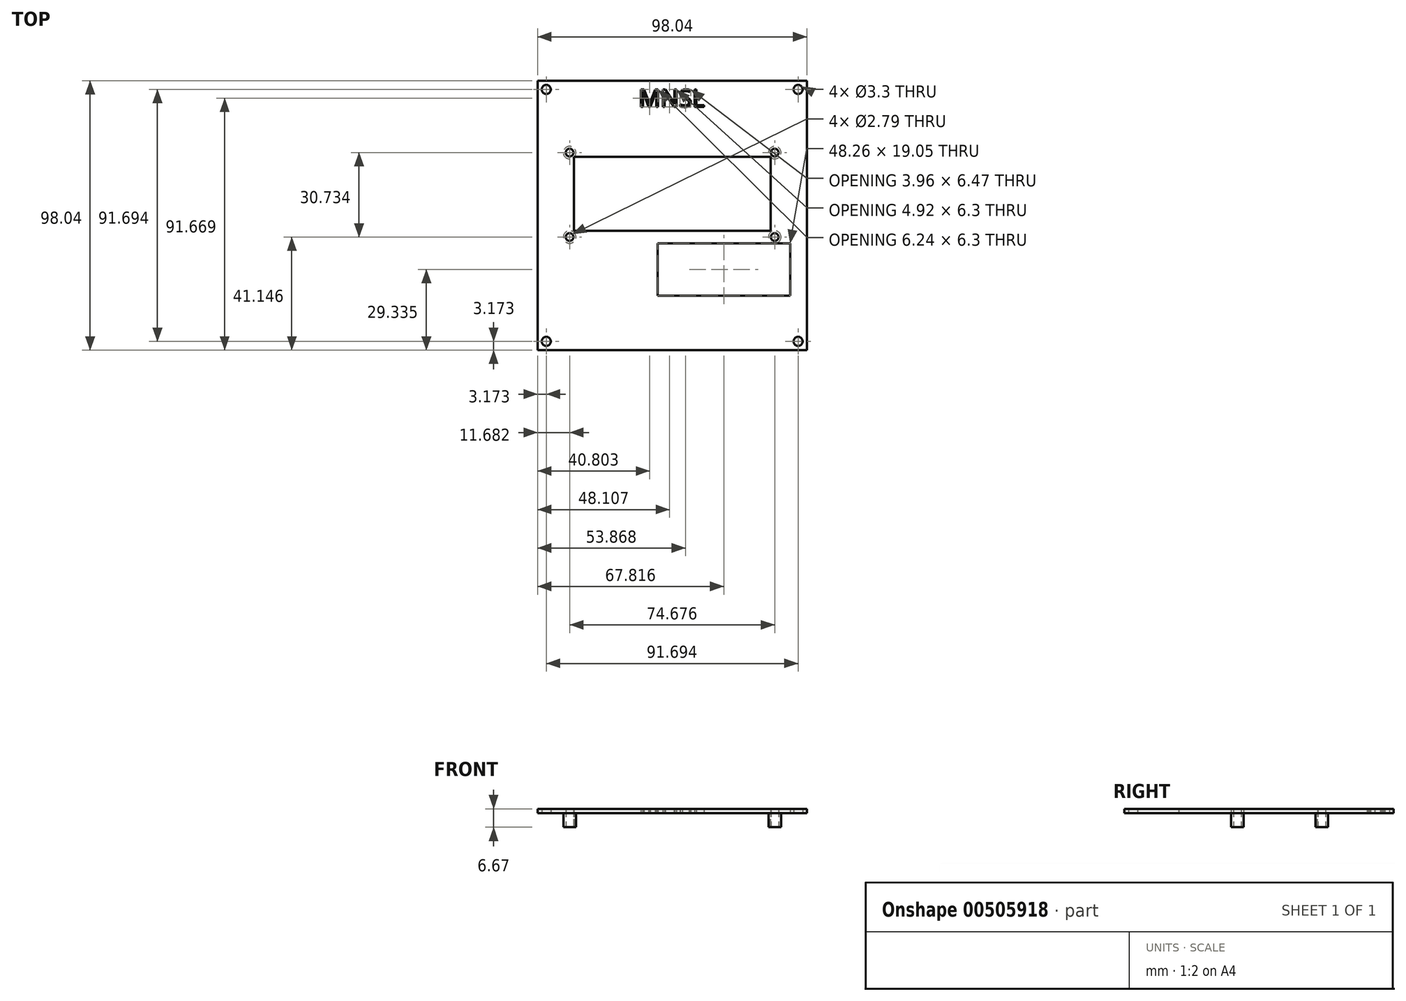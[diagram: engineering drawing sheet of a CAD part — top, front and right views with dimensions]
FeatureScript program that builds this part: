
annotation { "Feature Type Name" : "Feature", "Feature Type Description" : "" }
export const myFeature = defineFeature(function(context is Context, id is Id, definition is map)
    precondition{}
    {
        {
            var Q0;
            Q0=qCreatedBy(makeId("Top.planeOp"),FACE);
            var sketch = newSketch(context, id + "F0", { "sketchPlane" : qUnion([Q0])});
            skLineSegment(sketch, "E0.bottom", {"start": v(49.02, 49.02) * mm, "end": v(-49.02, 49.02) * mm});
            skLineSegment(sketch, "E0.top", {"start": v(49.02, -49.02) * mm, "end": v(-49.02, -49.02) * mm});
            skLineSegment(sketch, "E0.left", {"start": v(49.02, 49.02) * mm, "end": v(49.02, -49.02) * mm});
            skLineSegment(sketch, "E0.right", {"start": v(-49.02, 49.02) * mm, "end": v(-49.02, -49.02) * mm});
            skPoint(sketch, "E0.middle", {"position": v(0, 0) * mm});
            skLineSegment(sketch, "E1.bottom", {"start": v(49.02, 49.02) * mm, "end": v(42.67, 49.02) * mm, "construction": true});
            skLineSegment(sketch, "E1.top", {"start": v(49.02, 42.67) * mm, "end": v(42.67, 42.67) * mm, "construction": true});
            skLineSegment(sketch, "E1.left", {"start": v(49.02, 49.02) * mm, "end": v(49.02, 42.67) * mm, "construction": true});
            skLineSegment(sketch, "E1.right", {"start": v(42.67, 49.02) * mm, "end": v(42.67, 42.67) * mm, "construction": true});
            skLineSegment(sketch, "E2.bottom", {"start": v(-49.02, 49.02) * mm, "end": v(-42.67, 49.02) * mm, "construction": true});
            skLineSegment(sketch, "E2.top", {"start": v(-49.02, 42.67) * mm, "end": v(-42.67, 42.67) * mm, "construction": true});
            skLineSegment(sketch, "E2.left", {"start": v(-49.02, 49.02) * mm, "end": v(-49.02, 42.67) * mm, "construction": true});
            skLineSegment(sketch, "E2.right", {"start": v(-42.67, 49.02) * mm, "end": v(-42.67, 42.67) * mm, "construction": true});
            skLineSegment(sketch, "E3.bottom", {"start": v(-49.02, -49.02) * mm, "end": v(-42.67, -49.02) * mm, "construction": true});
            skLineSegment(sketch, "E3.top", {"start": v(-49.02, -42.67) * mm, "end": v(-42.67, -42.67) * mm, "construction": true});
            skLineSegment(sketch, "E3.left", {"start": v(-49.02, -49.02) * mm, "end": v(-49.02, -42.67) * mm, "construction": true});
            skLineSegment(sketch, "E3.right", {"start": v(-42.67, -49.02) * mm, "end": v(-42.67, -42.67) * mm, "construction": true});
            skLineSegment(sketch, "E4.bottom", {"start": v(49.02, -49.02) * mm, "end": v(42.67, -49.02) * mm, "construction": true});
            skLineSegment(sketch, "E4.top", {"start": v(49.02, -42.67) * mm, "end": v(42.67, -42.67) * mm, "construction": true});
            skLineSegment(sketch, "E4.left", {"start": v(49.02, -49.02) * mm, "end": v(49.02, -42.67) * mm, "construction": true});
            skLineSegment(sketch, "E4.right", {"start": v(42.67, -49.02) * mm, "end": v(42.67, -42.67) * mm, "construction": true});
            skLineSegment(sketch, "E5", {"start": v(-42.67, -42.67) * mm, "end": v(-49.02, -49.02) * mm, "construction": true});
            skLineSegment(sketch, "E6", {"start": v(-42.67, 42.67) * mm, "end": v(-49.02, 49.02) * mm, "construction": true});
            skLineSegment(sketch, "E7", {"start": v(49.02, 49.02) * mm, "end": v(42.67, 42.67) * mm, "construction": true});
            skLineSegment(sketch, "E8", {"start": v(49.02, -49.02) * mm, "end": v(42.67, -42.67) * mm, "construction": true});
            skCircle(sketch, "E9", {"center": v(45.85, -45.85) * mm, "radius": 1.65 * mm});
            skCircle(sketch, "E10", {"center": v(45.85, 45.85) * mm, "radius": 1.65 * mm});
            skCircle(sketch, "E11", {"center": v(-45.85, 45.85) * mm, "radius": 1.65 * mm});
            skCircle(sketch, "E12", {"center": v(-45.85, -45.85) * mm, "radius": 1.65 * mm});
            skLineSegment(sketch, "E13.bottom", {"start": v(39.88, 25.4) * mm, "end": v(-39.88, 25.4) * mm, "construction": true});
            skLineSegment(sketch, "E13.top", {"start": v(39.88, -25.4) * mm, "end": v(-39.88, -25.4) * mm, "construction": true});
            skLineSegment(sketch, "E13.left", {"start": v(39.88, 25.4) * mm, "end": v(39.88, -25.4) * mm, "construction": true});
            skLineSegment(sketch, "E13.right", {"start": v(-39.88, 25.4) * mm, "end": v(-39.88, -25.4) * mm, "construction": true});
            skLineSegment(sketch, "E14.bottom", {"start": v(-39.88, 25.4) * mm, "end": v(-37.34, 25.4) * mm, "construction": true});
            skLineSegment(sketch, "E14.top", {"start": v(-39.88, 22.86) * mm, "end": v(-37.34, 22.86) * mm, "construction": true});
            skLineSegment(sketch, "E14.left", {"start": v(-39.88, 25.4) * mm, "end": v(-39.88, 22.86) * mm, "construction": true});
            skLineSegment(sketch, "E14.right", {"start": v(-37.34, 25.4) * mm, "end": v(-37.34, 22.86) * mm, "construction": true});
            skCircle(sketch, "E15", {"center": v(-37.34, 22.86) * mm, "radius": 1.4 * mm});
            skLineSegment(sketch, "E16.bottom", {"start": v(-37.34, 22.86) * mm, "end": v(37.34, 22.86) * mm, "construction": true});
            skLineSegment(sketch, "E16.top", {"start": v(-37.34, -7.87) * mm, "end": v(37.34, -7.87) * mm, "construction": true});
            skLineSegment(sketch, "E16.left", {"start": v(-37.34, 22.86) * mm, "end": v(-37.34, -7.87) * mm, "construction": true});
            skLineSegment(sketch, "E16.right", {"start": v(37.34, 22.86) * mm, "end": v(37.34, -7.87) * mm, "construction": true});
            skCircle(sketch, "E17", {"center": v(37.34, 22.86) * mm, "radius": 1.4 * mm});
            skCircle(sketch, "E18", {"center": v(-37.34, -7.87) * mm, "radius": 1.4 * mm});
            skCircle(sketch, "E19", {"center": v(-37.34, 22.86) * mm, "radius": 2.29 * mm});
            skCircle(sketch, "E20", {"center": v(-37.34, -7.87) * mm, "radius": 2.29 * mm});
            skCircle(sketch, "E21", {"center": v(37.34, 22.86) * mm, "radius": 2.29 * mm});
            skLineSegment(sketch, "E22.bottom", {"start": v(-39.88, 25.4) * mm, "end": v(-35.81, 25.4) * mm, "construction": true});
            skLineSegment(sketch, "E22.top", {"start": v(-39.88, 21.34) * mm, "end": v(-35.81, 21.34) * mm, "construction": true});
            skLineSegment(sketch, "E22.left", {"start": v(-39.88, 25.4) * mm, "end": v(-39.88, 21.34) * mm, "construction": true});
            skLineSegment(sketch, "E22.right", {"start": v(-35.81, 25.4) * mm, "end": v(-35.81, 21.34) * mm, "construction": true});
            skLineSegment(sketch, "E23.bottom", {"start": v(-35.81, 21.34) * mm, "end": v(35.81, 21.34) * mm});
            skLineSegment(sketch, "E23.top", {"start": v(-35.81, -5.59) * mm, "end": v(35.81, -5.59) * mm});
            skLineSegment(sketch, "E23.left", {"start": v(-35.81, 21.34) * mm, "end": v(-35.81, -5.59) * mm});
            skLineSegment(sketch, "E23.right", {"start": v(35.81, 21.34) * mm, "end": v(35.81, -5.59) * mm});
            skLineSegment(sketch, "E24", {"start": v(-35.81, -5.59) * mm, "end": v(-5.33, -5.59) * mm, "construction": true});
            skLineSegment(sketch, "E25.bottom", {"start": v(-5.33, -10.16) * mm, "end": v(42.93, -10.16) * mm});
            skLineSegment(sketch, "E25.top", {"start": v(-5.33, -29.21) * mm, "end": v(42.93, -29.21) * mm});
            skLineSegment(sketch, "E25.left", {"start": v(-5.33, -10.16) * mm, "end": v(-5.33, -29.21) * mm});
            skLineSegment(sketch, "E25.right", {"start": v(42.93, -10.16) * mm, "end": v(42.93, -29.21) * mm});
            skLineSegment(sketch, "E26", {"start": v(-45.85, 45.85) * mm, "end": v(45.85, 45.85) * mm, "construction": true});
            skLineSegment(sketch, "E27", {"start": v(-45.85, 45.85) * mm, "end": v(-45.85, -45.85) * mm, "construction": true});
            skCircle(sketch, "E28", {"center": v(37.34, -7.87) * mm, "radius": 1.4 * mm});
            skCircle(sketch, "E29", {"center": v(37.34, -7.87) * mm, "radius": 2.29 * mm});
            skLineSegment(sketch, "E30", {"start": v(-5.33, -5.59) * mm, "end": v(-5.33, -10.16) * mm, "construction": true});
            skText(sketch, "E31", { "text": "MNSL", "fontName": "OpenSans-Regular.ttf"});
            const initialGuessF0  = {"E31": [-0.0122, 0.0395, 1, 0, 0.00635]};
            skSetInitialGuess(sketch, initialGuessF0);
            skSolve(sketch);
        }
        {
            var Q0;
            Q0=makeQuery(id+"F0.imprint","IMPRINT",FACE,{"disambiguationData":[TD([[makeQuery(id+"F0.imprint","IMPRINT",EDGE,{"derivedFrom":sQuery(id+"F0.wireOp",EDGE,"E17")}),-1.0]])]});
            var Q1;
            Q1=makeQuery(id+"F0.imprint","IMPRINT",FACE,{"disambiguationData":[TD([[makeQuery(id+"F0.imprint","IMPRINT",EDGE,{"derivedFrom":sQuery(id+"F0.wireOp",EDGE,"E15")}),-1.0]])]});
            var Q2;
            Q2=makeQuery(id+"F0.imprint","IMPRINT",FACE,{"disambiguationData":[TD([[makeQuery(id+"F0.imprint","IMPRINT",EDGE,{"derivedFrom":sQuery(id+"F0.wireOp",EDGE,"E18")}),-1.0]])]});
            var Q3;
            Q3=makeQuery(id+"F0.imprint","IMPRINT",FACE,{"disambiguationData":[TD([[makeQuery(id+"F0.imprint","IMPRINT",EDGE,{"derivedFrom":sQuery(id+"F0.wireOp",EDGE,"E28")}),-1.0]])]});
            var Q4;
            Q4=makeQuery(id+"F0.imprint","IMPRINT",FACE,{"disambiguationData":[TD([[makeQuery(id+"F0.imprint","IMPRINT",EDGE,{"derivedFrom":sQuery(id+"F0.wireOp",EDGE,"E0.bottom")}),1.0]])]});
            extrude(context, id + "F1", {"entities" : qUnion([Q0, Q1, Q2, Q3, Q4]), "depth" : 1.59 * mm});
        }
        {
            var Q0;
            Q0=makeQuery(id+"F0.imprint","IMPRINT",FACE,{"disambiguationData":[TD([[makeQuery(id+"F0.imprint","IMPRINT",EDGE,{"derivedFrom":sQuery(id+"F0.wireOp",EDGE,"E17")}),-1.0]])]});
            var Q1;
            Q1=makeQuery(id+"F0.imprint","IMPRINT",FACE,{"disambiguationData":[TD([[makeQuery(id+"F0.imprint","IMPRINT",EDGE,{"derivedFrom":sQuery(id+"F0.wireOp",EDGE,"E18")}),-1.0]])]});
            var Q2;
            Q2=makeQuery(id+"F0.imprint","IMPRINT",FACE,{"disambiguationData":[TD([[makeQuery(id+"F0.imprint","IMPRINT",EDGE,{"derivedFrom":sQuery(id+"F0.wireOp",EDGE,"E15")}),-1.0]])]});
            var Q3;
            Q3=makeQuery(id+"F0.imprint","IMPRINT",FACE,{"disambiguationData":[TD([[makeQuery(id+"F0.imprint","IMPRINT",EDGE,{"derivedFrom":sQuery(id+"F0.wireOp",EDGE,"E28")}),-1.0]])]});
            extrude(context, id + "F2", {"entities" : qUnion([Q0, Q1, Q2, Q3]), "operationType" : NewBodyOperationType.ADD, "oppositeDirection" : true, "depth" : 5.08 * mm});
        }
    });
